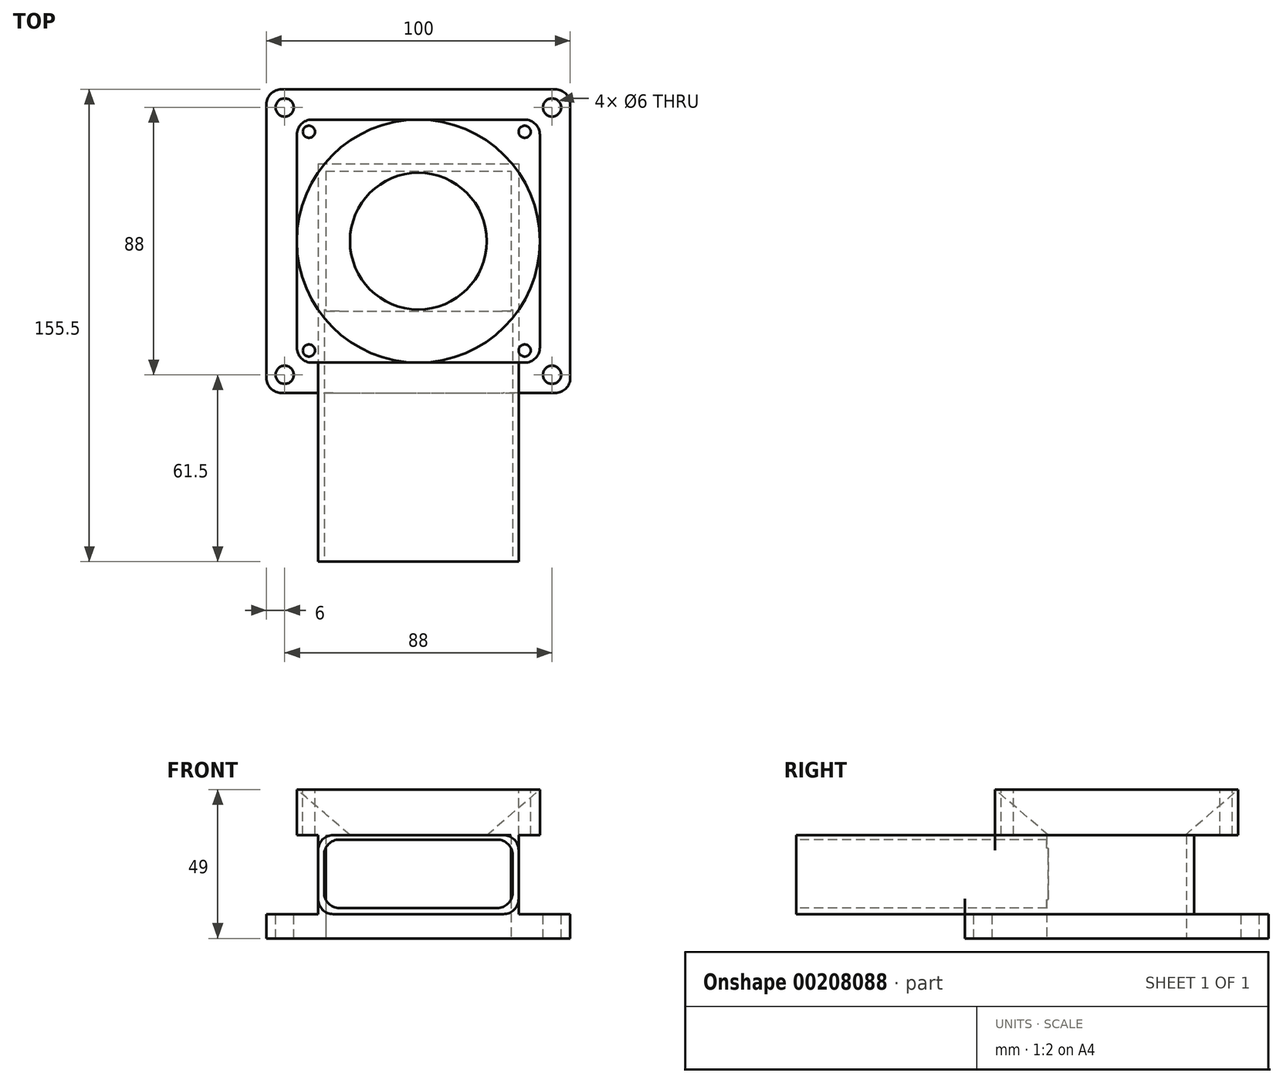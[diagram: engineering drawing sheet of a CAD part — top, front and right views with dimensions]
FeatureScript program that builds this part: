
annotation { "Feature Type Name" : "Feature", "Feature Type Description" : "" }
export const myFeature = defineFeature(function(context is Context, id is Id, definition is map)
    precondition{}
    {
        {
            var Q0;
            Q0=qCreatedBy(makeId("Top.planeOp"),FACE);
            var sketch = newSketch(context, id + "F0", { "sketchPlane" : qUnion([Q0])});
            skLineSegment(sketch, "E0.bottom", {"start": v(-30.5, 23) * mm, "end": v(30.5, 23) * mm});
            skLineSegment(sketch, "E0.top", {"start": v(-30.5, -23) * mm, "end": v(30.5, -23) * mm});
            skLineSegment(sketch, "E0.left", {"start": v(-30.5, 23) * mm, "end": v(-30.5, -23) * mm});
            skLineSegment(sketch, "E0.right", {"start": v(30.5, 23) * mm, "end": v(30.5, -23) * mm});
            skPoint(sketch, "E0.middle", {"position": v(0, 0) * mm});
            skLineSegment(sketch, "E1.bottom", {"start": v(-50, 50) * mm, "end": v(50, 50) * mm});
            skLineSegment(sketch, "E1.top", {"start": v(-50, -50) * mm, "end": v(50, -50) * mm});
            skLineSegment(sketch, "E1.left", {"start": v(-50, 50) * mm, "end": v(-50, -50) * mm});
            skLineSegment(sketch, "E1.right", {"start": v(50, 50) * mm, "end": v(50, -50) * mm});
            skSolve(sketch);
        }
        {
            var Q0;
            Q0=makeQuery(id+"F0.imprint","IMPRINT",FACE,{"disambiguationData":[TD([[makeQuery(id+"F0.imprint","IMPRINT",EDGE,{"derivedFrom":sQuery(id+"F0.wireOp",EDGE,"E0.bottom")}),1.0]])]});
            extrude(context, id + "F1", {"entities" : qUnion([Q0]), "depth" : 8 * mm});
        }
        {
            var Q0;
            Q0=makeQuery(id+"F1.opExtrude","CAP_FACE",FACE,{"disambiguationData":[OSD([sQuery(id+"F0.wireOp",EDGE,"E0.bottom"),sQuery(id+"F0.wireOp",EDGE,"E0.top"),sQuery(id+"F0.wireOp",EDGE,"E0.left"),sQuery(id+"F0.wireOp",EDGE,"E0.right"),sQuery(id+"F0.wireOp",EDGE,"E1.bottom"),sQuery(id+"F0.wireOp",EDGE,"E1.top"),sQuery(id+"F0.wireOp",EDGE,"E1.left"),sQuery(id+"F0.wireOp",EDGE,"E1.right")])],"isStart":false});
            var sketch = newSketch(context, id + "F2", { "sketchPlane" : qUnion([Q0])});
            skLineSegment(sketch, "E2.bottom", {"start": v(-30.5, 23) * mm, "end": v(30.5, 23) * mm});
            skLineSegment(sketch, "E2.top", {"start": v(-30.5, -23) * mm, "end": v(30.5, -23) * mm});
            skLineSegment(sketch, "E2.left", {"start": v(-30.5, 23) * mm, "end": v(-30.5, -23) * mm});
            skLineSegment(sketch, "E2.right", {"start": v(30.5, 23) * mm, "end": v(30.5, -23) * mm});
            skPoint(sketch, "E2.middle", {"position": v(0, 0) * mm});
            skLineSegment(sketch, "E3.bottom", {"start": v(-33, 25.5) * mm, "end": v(33, 25.5) * mm});
            skLineSegment(sketch, "E3.top", {"start": v(-33, -25.5) * mm, "end": v(33, -25.5) * mm});
            skLineSegment(sketch, "E3.left", {"start": v(-33, 25.5) * mm, "end": v(-33, -25.5) * mm});
            skLineSegment(sketch, "E3.right", {"start": v(33, 25.5) * mm, "end": v(33, -25.5) * mm});
            skSolve(sketch);
        }
        {
            var Q0;
            Q0 = qSketchRegion(id + "F2", true);
            extrude(context, id + "F3", {"entities" : qUnion([Q0]), "operationType" : NewBodyOperationType.ADD, "depth" : 26 * mm});
        }
        {
            var Q0;
            Q0=makeQuery(id+"F3.opExtrude","CAP_FACE",FACE,{"disambiguationData":[OSD([sQuery(id+"F2.wireOp",EDGE,"E2.bottom"),sQuery(id+"F2.wireOp",EDGE,"E2.top"),sQuery(id+"F2.wireOp",EDGE,"E2.left"),sQuery(id+"F2.wireOp",EDGE,"E2.right"),sQuery(id+"F2.wireOp",EDGE,"E3.bottom"),sQuery(id+"F2.wireOp",EDGE,"E3.top"),sQuery(id+"F2.wireOp",EDGE,"E3.left"),sQuery(id+"F2.wireOp",EDGE,"E3.right")])],"isStart":false});
            var sketch = newSketch(context, id + "F4", { "sketchPlane" : qUnion([Q0])});
            skLineSegment(sketch, "E4.bottom", {"start": v(-40, 40) * mm, "end": v(40, 40) * mm});
            skLineSegment(sketch, "E4.top", {"start": v(-40, -40) * mm, "end": v(40, -40) * mm});
            skLineSegment(sketch, "E4.left", {"start": v(-40, 40) * mm, "end": v(-40, -40) * mm});
            skLineSegment(sketch, "E4.right", {"start": v(40, 40) * mm, "end": v(40, -40) * mm});
            skPoint(sketch, "E4.middle", {"position": v(0, 0) * mm});
            skSolve(sketch);
        }
        {
            var Q0;
            Q0 = qSketchRegion(id + "F4", true);
            extrude(context, id + "F5", {"entities" : qUnion([Q0]), "operationType" : NewBodyOperationType.ADD, "depth" : 15 * mm});
        }
        {
            var Q0;
            Q0=makeQuery(id+"F5.boolean.opBoolean","SPLIT",FACE,{"disambiguationData":[TD([makeQuery(id+"F1.opExtrude","SWEPT_FACE",FACE,{"disambiguationData":[OSD([sQuery(id+"F0.wireOp",EDGE,"E0.bottom")])]})])],"derivedFrom":makeQuery(id+"F5.opExtrude","CAP_FACE",FACE,{"disambiguationData":[OSD([sQuery(id+"F4.wireOp",EDGE,"E4.bottom"),sQuery(id+"F4.wireOp",EDGE,"E4.top"),sQuery(id+"F4.wireOp",EDGE,"E4.left"),sQuery(id+"F4.wireOp",EDGE,"E4.right")])],"isStart":true})});
            var sketch = newSketch(context, id + "F6", { "sketchPlane" : qUnion([Q0])});
            skCircle(sketch, "E5", {"center": v(0, 0) * mm, "radius": 22.5 * mm});
            skSolve(sketch);
        }
        {
            var Q0;
            Q0=makeQuery(id+"F5.opExtrude","CAP_FACE",FACE,{"disambiguationData":[OSD([sQuery(id+"F4.wireOp",EDGE,"E4.bottom"),sQuery(id+"F4.wireOp",EDGE,"E4.top"),sQuery(id+"F4.wireOp",EDGE,"E4.left"),sQuery(id+"F4.wireOp",EDGE,"E4.right")])],"isStart":false});
            var sketch = newSketch(context, id + "F7", { "sketchPlane" : qUnion([Q0])});
            skCircle(sketch, "E6", {"center": v(0, 0) * mm, "radius": 40 * mm});
            skSolve(sketch);
        }
        {
            var Q1;
            {var subQ0=sQuery(id+"F7.wireOp",EDGE,"E6");var subQ1=makeQuery(id+"F7.imprint","INTERSECT",VERTEX,{"derivedFrom":[makeQuery(id+"F5.opExtrude","CAP_EDGE",EDGE,{"disambiguationData":[OSD([sQuery(id+"F4.wireOp",EDGE,"E4.bottom")])],"isStart":false}),subQ0]});Q1=makeQuery(id+"F7.imprint","IMPRINT",FACE,{"disambiguationData":[TD([[makeQuery(id+"F7.imprint","IMPRINT",EDGE,{"disambiguationData":[TD([[subQ1,1.0]])],"derivedFrom":subQ0}),1.0]])]});}
            var Q2;
            {var subQ0=sQuery(id+"F6.wireOp",EDGE,"E5");var subQ1=makeQuery(id+"F6.imprint","INTERSECT",VERTEX,{"derivedFrom":[makeQuery(id+"F3.opExtrude","CAP_EDGE",EDGE,{"disambiguationData":[OSD([sQuery(id+"F2.wireOp",EDGE,"E2.bottom")])],"isStart":false}),subQ0]});Q2=makeQuery(id+"F6.imprint","IMPRINT",FACE,{"disambiguationData":[TD([[makeQuery(id+"F6.imprint","IMPRINT",EDGE,{"disambiguationData":[TD([[subQ1,1.0]])],"derivedFrom":subQ0}),1.0]])]});}
            loft(context, id + "F8", {"operationType" : NewBodyOperationType.REMOVE, "sheetProfilesArray" : [{ "sheetProfileEntities" : qUnion([Q1]) }, { "sheetProfileEntities" : qUnion([Q2]) }]});
        }
        {
            var Q0;
            Q0=makeQuery(id+"F3.opExtrude","SWEPT_FACE",FACE,{"disambiguationData":[OSD([sQuery(id+"F2.wireOp",EDGE,"E3.top")])]});
            var sketch = newSketch(context, id + "F9", { "sketchPlane" : qUnion([Q0])});
            skLineSegment(sketch, "E7.bottom", {"start": v(-33, 34) * mm, "end": v(33, 34) * mm});
            skLineSegment(sketch, "E7.top", {"start": v(-33, 8) * mm, "end": v(33, 8) * mm});
            skLineSegment(sketch, "E7.left", {"start": v(-33, 34) * mm, "end": v(-33, 8) * mm});
            skLineSegment(sketch, "E7.right", {"start": v(33, 34) * mm, "end": v(33, 8) * mm});
            skSolve(sketch);
        }
        {
            var Q0;
            Q0 = qSketchRegion(id + "F9", true);
            extrude(context, id + "F10", {"entities" : qUnion([Q0]), "operationType" : NewBodyOperationType.ADD, "depth" : 80 * mm});
        }
        {
            var Q0;
            Q0=makeQuery(id+"F10.opExtrude","CAP_FACE",FACE,{"disambiguationData":[OSD([sQuery(id+"F9.wireOp",EDGE,"E7.bottom"),sQuery(id+"F9.wireOp",EDGE,"E7.top"),sQuery(id+"F9.wireOp",EDGE,"E7.left"),sQuery(id+"F9.wireOp",EDGE,"E7.right")])],"isStart":false});
            var sketch = newSketch(context, id + "F11", { "sketchPlane" : qUnion([Q0])});
            skLineSegment(sketch, "E8.bottom", {"start": v(31, 10) * mm, "end": v(-31, 10) * mm});
            skLineSegment(sketch, "E8.top", {"start": v(31, 32.5) * mm, "end": v(-31, 32.5) * mm});
            skLineSegment(sketch, "E8.left", {"start": v(31, 10) * mm, "end": v(31, 32.5) * mm});
            skLineSegment(sketch, "E8.right", {"start": v(-31, 10) * mm, "end": v(-31, 32.5) * mm});
            skSolve(sketch);
        }
        {
            var Q0;
            Q0 = qSketchRegion(id + "F11", true);
            extrude(context, id + "F12", {"entities" : qUnion([Q0]), "operationType" : NewBodyOperationType.REMOVE, "oppositeDirection" : true, "depth" : 83 * mm});
        }
        {
            var Q0;
            Q0=makeQuery(id+"F12.boolean.opBoolean","COPY",EDGE,{"derivedFrom":makeQuery(id+"F12.opExtrude","SWEPT_EDGE",EDGE,{"disambiguationData":[OSD([sQuery(id+"F11.wireOp",EDGE,"E8.top"),sQuery(id+"F11.wireOp",EDGE,"E8.right")])]})});
            var Q1;
            Q1=makeQuery(id+"F12.boolean.opBoolean","COPY",EDGE,{"derivedFrom":makeQuery(id+"F12.opExtrude","SWEPT_EDGE",EDGE,{"disambiguationData":[OSD([sQuery(id+"F11.wireOp",EDGE,"E8.bottom"),sQuery(id+"F11.wireOp",EDGE,"E8.right")])]})});
            var Q2;
            Q2=makeQuery(id+"F12.boolean.opBoolean","COPY",EDGE,{"derivedFrom":makeQuery(id+"F12.opExtrude","SWEPT_EDGE",EDGE,{"disambiguationData":[OSD([sQuery(id+"F11.wireOp",EDGE,"E8.top"),sQuery(id+"F11.wireOp",EDGE,"E8.left")])]})});
            var Q3;
            Q3=makeQuery(id+"F12.boolean.opBoolean","COPY",EDGE,{"derivedFrom":makeQuery(id+"F12.opExtrude","SWEPT_EDGE",EDGE,{"disambiguationData":[OSD([sQuery(id+"F11.wireOp",EDGE,"E8.bottom"),sQuery(id+"F11.wireOp",EDGE,"E8.left")])]})});
            fillet(context, id + "F13", {"entities" : qUnion([Q0, Q1, Q2, Q3]), "radius" : 5 * mm, "tangentPropagation" : true, "allowEdgeOverflow" : false});
        }
        {
            var Q0;
            Q0=makeQuery(id+"F1.opExtrude","SWEPT_EDGE",EDGE,{"disambiguationData":[OSD([sQuery(id+"F0.wireOp",EDGE,"E1.bottom"),sQuery(id+"F0.wireOp",EDGE,"E1.right")])]});
            var Q1;
            Q1=makeQuery(id+"F1.opExtrude","SWEPT_EDGE",EDGE,{"disambiguationData":[OSD([sQuery(id+"F0.wireOp",EDGE,"E1.top"),sQuery(id+"F0.wireOp",EDGE,"E1.right")])]});
            var Q2;
            Q2=makeQuery(id+"F5.opExtrude","SWEPT_EDGE",EDGE,{"disambiguationData":[OSD([sQuery(id+"F4.wireOp",EDGE,"E4.top"),sQuery(id+"F4.wireOp",EDGE,"E4.right")])]});
            var Q3;
            Q3=makeQuery(id+"F5.opExtrude","SWEPT_EDGE",EDGE,{"disambiguationData":[OSD([sQuery(id+"F4.wireOp",EDGE,"E4.bottom"),sQuery(id+"F4.wireOp",EDGE,"E4.right")])]});
            var Q4;
            Q4=makeQuery(id+"F5.opExtrude","SWEPT_EDGE",EDGE,{"disambiguationData":[OSD([sQuery(id+"F4.wireOp",EDGE,"E4.top"),sQuery(id+"F4.wireOp",EDGE,"E4.left")])]});
            var Q5;
            Q5=makeQuery(id+"F5.opExtrude","SWEPT_EDGE",EDGE,{"disambiguationData":[OSD([sQuery(id+"F4.wireOp",EDGE,"E4.bottom"),sQuery(id+"F4.wireOp",EDGE,"E4.left")])]});
            var Q6;
            Q6=makeQuery(id+"F1.opExtrude","SWEPT_EDGE",EDGE,{"disambiguationData":[OSD([sQuery(id+"F0.wireOp",EDGE,"E1.top"),sQuery(id+"F0.wireOp",EDGE,"E1.left")])]});
            var Q7;
            Q7=makeQuery(id+"F1.opExtrude","SWEPT_EDGE",EDGE,{"disambiguationData":[OSD([sQuery(id+"F0.wireOp",EDGE,"E1.bottom"),sQuery(id+"F0.wireOp",EDGE,"E1.left")])]});
            fillet(context, id + "F14", {"entities" : qUnion([Q0, Q1, Q2, Q3, Q4, Q5, Q6, Q7]), "radius" : 5 * mm, "tangentPropagation" : true, "allowEdgeOverflow" : false});
        }
        {
            var Q0;
            Q0=makeQuery(id+"F1.opExtrude","CAP_FACE",FACE,{"disambiguationData":[OSD([sQuery(id+"F0.wireOp",EDGE,"E0.bottom"),sQuery(id+"F0.wireOp",EDGE,"E0.top"),sQuery(id+"F0.wireOp",EDGE,"E0.left"),sQuery(id+"F0.wireOp",EDGE,"E0.right"),sQuery(id+"F0.wireOp",EDGE,"E1.bottom"),sQuery(id+"F0.wireOp",EDGE,"E1.top"),sQuery(id+"F0.wireOp",EDGE,"E1.left"),sQuery(id+"F0.wireOp",EDGE,"E1.right")])],"isStart":false});
            var sketch = newSketch(context, id + "F15", { "sketchPlane" : qUnion([Q0])});
            skPoint(sketch, "E9", {"position": v(44, 44) * mm});
            skPoint(sketch, "E10", {"position": v(44, -44) * mm});
            skPoint(sketch, "E11", {"position": v(-44, -44) * mm});
            skPoint(sketch, "E12", {"position": v(-44, 44) * mm});
            skSolve(sketch);
        }
        {
            var Q0;
            Q0=sQuery(id+"F15.wireOp",VERTEX,"E9");
            var Q1;
            Q1=sQuery(id+"F15.wireOp",VERTEX,"E10");
            var Q2;
            Q2=sQuery(id+"F15.wireOp",VERTEX,"E11");
            var Q3;
            Q3=sQuery(id+"F15.wireOp",VERTEX,"E12");
            var Q4;
            Q4=makeQuery(id+"F1.opExtrude","SWEPT_BODY",BODY,{"disambiguationData":[OSD([sQuery(id+"F0.wireOp",EDGE,"E0.bottom"),sQuery(id+"F0.wireOp",EDGE,"E0.top"),sQuery(id+"F0.wireOp",EDGE,"E0.left"),sQuery(id+"F0.wireOp",EDGE,"E0.right"),sQuery(id+"F0.wireOp",EDGE,"E1.bottom"),sQuery(id+"F0.wireOp",EDGE,"E1.top"),sQuery(id+"F0.wireOp",EDGE,"E1.left"),sQuery(id+"F0.wireOp",EDGE,"E1.right")])]});
            hole(context, id + "F16", {"style" : HoleStyle.SIMPLE, "endStyle" : HoleEndStyle.BLIND, "holeDiameter" : 6 * mm, "holeDepth" : 16 * mm, "startFromSketch" : true, "locations" : qUnion([Q0, Q1, Q2, Q3]), "scope" : qUnion([Q4])});
        }
        {
            var Q0;
            {var subQ0=sQuery(id+"F4.wireOp",EDGE,"E4.bottom");var subQ1=sQuery(id+"F4.wireOp",EDGE,"E4.right");var subQ2=makeQuery(id+"F5.opExtrude","CAP_FACE",FACE,{"disambiguationData":[OSD([subQ0,sQuery(id+"F4.wireOp",EDGE,"E4.top"),sQuery(id+"F4.wireOp",EDGE,"E4.left"),subQ1])],"isStart":false});Q0=makeQuery(id+"F8.boolean.opBoolean","SPLIT",FACE,{"disambiguationData":[TD([makeQuery(id+"F5.opExtrude","SWEPT_FACE",FACE,{"disambiguationData":[OSD([subQ0])]}),subQ2,makeQuery(id+"F5.opExtrude","SWEPT_FACE",FACE,{"disambiguationData":[OSD([subQ1])]}),makeQuery(id+"F8.opLoft","SWEPT_FACE",FACE,{"disambiguationData":[OSD([subQ0,subQ1,sQuery(id+"F6.wireOp",EDGE,"E5"),sQuery(id+"F7.wireOp",EDGE,"E6")])]})])],"derivedFrom":subQ2});}
            var sketch = newSketch(context, id + "F17", { "sketchPlane" : qUnion([Q0])});
            skPoint(sketch, "E13", {"position": v(35, 36) * mm});
            skPoint(sketch, "E14", {"position": v(35, -36) * mm});
            skPoint(sketch, "E15", {"position": v(-36, -36) * mm});
            skPoint(sketch, "E16", {"position": v(-36, 36) * mm});
            skSolve(sketch);
        }
        {
            var Q0;
            Q0=sQuery(id+"F17.wireOp",VERTEX,"E13");
            var Q1;
            Q1=sQuery(id+"F17.wireOp",VERTEX,"E14");
            var Q2;
            Q2=sQuery(id+"F17.wireOp",VERTEX,"E15");
            var Q3;
            Q3=sQuery(id+"F17.wireOp",VERTEX,"E16");
            var Q4;
            Q4=makeQuery(id+"F1.opExtrude","SWEPT_BODY",BODY,{"disambiguationData":[OSD([sQuery(id+"F0.wireOp",EDGE,"E0.bottom"),sQuery(id+"F0.wireOp",EDGE,"E0.top"),sQuery(id+"F0.wireOp",EDGE,"E0.left"),sQuery(id+"F0.wireOp",EDGE,"E0.right"),sQuery(id+"F0.wireOp",EDGE,"E1.bottom"),sQuery(id+"F0.wireOp",EDGE,"E1.top"),sQuery(id+"F0.wireOp",EDGE,"E1.left"),sQuery(id+"F0.wireOp",EDGE,"E1.right")])]});
            hole(context, id + "F18", {"style" : HoleStyle.SIMPLE, "endStyle" : HoleEndStyle.BLIND, "holeDiameter" : 4 * mm, "holeDepth" : 16 * mm, "startFromSketch" : true, "locations" : qUnion([Q0, Q1, Q2, Q3]), "scope" : qUnion([Q4])});
        }
        {
            var Q0;
            Q0=makeQuery(id+"F10.boolean.opBoolean","SPLIT",EDGE,{"derivedFrom":makeQuery(id+"F10.opExtrude","SWEPT_EDGE",EDGE,{"disambiguationData":[OSD([sQuery(id+"F9.wireOp",EDGE,"E7.bottom"),sQuery(id+"F9.wireOp",EDGE,"E7.left")])]})});
            var Q1;
            Q1=makeQuery(id+"F10.boolean.opBoolean","SPLIT",EDGE,{"derivedFrom":makeQuery(id+"F10.opExtrude","SWEPT_EDGE",EDGE,{"disambiguationData":[OSD([sQuery(id+"F9.wireOp",EDGE,"E7.top"),sQuery(id+"F9.wireOp",EDGE,"E7.left")])]})});
            var Q2;
            Q2=makeQuery(id+"F10.boolean.opBoolean","SPLIT",EDGE,{"derivedFrom":makeQuery(id+"F10.opExtrude","SWEPT_EDGE",EDGE,{"disambiguationData":[OSD([sQuery(id+"F9.wireOp",EDGE,"E7.top"),sQuery(id+"F9.wireOp",EDGE,"E7.right")])]})});
            var Q3;
            Q3=makeQuery(id+"F10.boolean.opBoolean","SPLIT",EDGE,{"derivedFrom":makeQuery(id+"F10.opExtrude","SWEPT_EDGE",EDGE,{"disambiguationData":[OSD([sQuery(id+"F9.wireOp",EDGE,"E7.bottom"),sQuery(id+"F9.wireOp",EDGE,"E7.right")])]})});
            fillet(context, id + "F19", {"entities" : qUnion([Q0, Q1, Q2, Q3]), "radius" : 5 * mm, "tangentPropagation" : true, "allowEdgeOverflow" : false});
        }
    });
